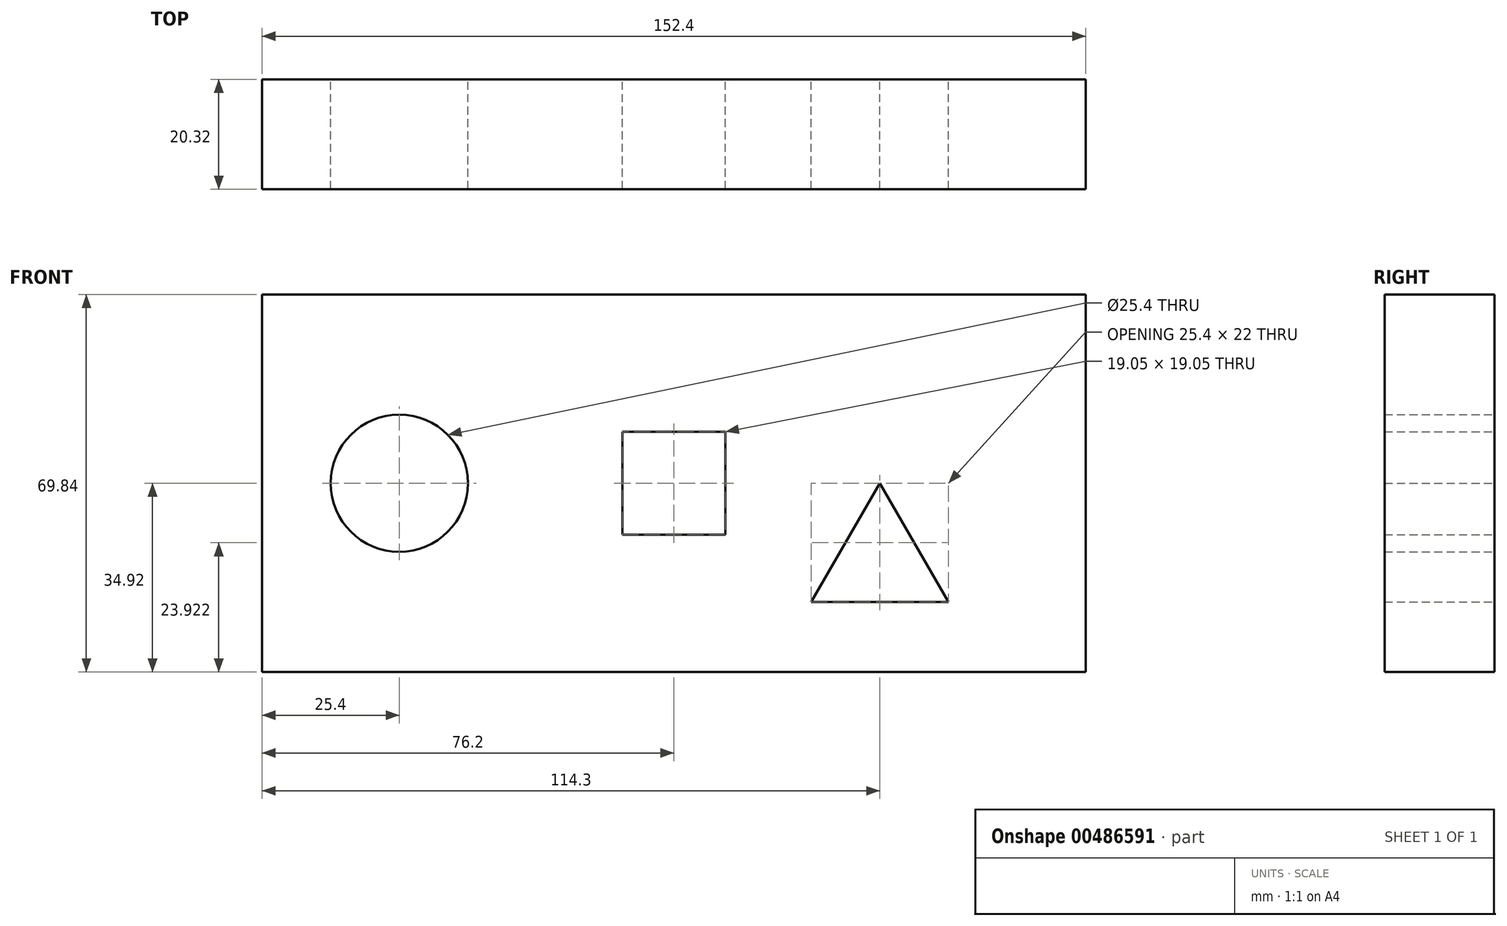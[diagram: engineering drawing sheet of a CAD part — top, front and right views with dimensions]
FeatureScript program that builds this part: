
annotation { "Feature Type Name" : "Feature", "Feature Type Description" : "" }
export const myFeature = defineFeature(function(context is Context, id is Id, definition is map)
    precondition{}
    {
        {
            var Q0;
            Q0=qCreatedBy(makeId("Front.planeOp"),FACE);
            var sketch = newSketch(context, id + "F0", { "sketchPlane" : qUnion([Q0])});
            skPoint(sketch, "E0", {"position": v(-31.75, 0) * mm});
            skPoint(sketch, "E1", {"position": v(-82.55, 0) * mm});
            skPoint(sketch, "E2", {"position": v(6.35, 0) * mm});
            skPoint(sketch, "E3", {"position": v(44.45, 0) * mm});
            skLineSegment(sketch, "E4.bottom", {"start": v(-22.22, 9.53) * mm, "end": v(-41.27, 9.53) * mm});
            skLineSegment(sketch, "E4.top", {"start": v(-22.22, -9.53) * mm, "end": v(-41.28, -9.52) * mm});
            skLineSegment(sketch, "E4.left", {"start": v(-22.22, 9.53) * mm, "end": v(-22.23, -9.53) * mm});
            skLineSegment(sketch, "E4.right", {"start": v(-41.27, 9.53) * mm, "end": v(-41.27, -9.52) * mm});
            skCircle(sketch, "E5", {"center": v(-82.55, 0) * mm, "radius": 12.7 * mm});
            skLineSegment(sketch, "E6", {"start": v(6.35, 0) * mm, "end": v(-6.35, -22) * mm});
            skLineSegment(sketch, "E7", {"start": v(-6.35, -22) * mm, "end": v(19.05, -22) * mm});
            skLineSegment(sketch, "E8", {"start": v(19.05, -22) * mm, "end": v(6.35, 0) * mm});
            skLineSegment(sketch, "E9.bottom", {"start": v(44.45, 34.92) * mm, "end": v(-107.95, 34.92) * mm});
            skLineSegment(sketch, "E9.top", {"start": v(44.45, -34.92) * mm, "end": v(-107.95, -34.92) * mm});
            skLineSegment(sketch, "E9.left", {"start": v(44.45, 34.92) * mm, "end": v(44.45, -34.92) * mm});
            skLineSegment(sketch, "E9.right", {"start": v(-107.95, 34.92) * mm, "end": v(-107.95, -34.92) * mm});
            skSolve(sketch);
        }
        {
            var Q0;
            Q0=makeQuery(id+"F0.imprint","IMPRINT",FACE,{"disambiguationData":[TD([[makeQuery(id+"F0.imprint","IMPRINT",EDGE,{"derivedFrom":sQuery(id+"F0.wireOp",EDGE,"E4.bottom")}),-1.0]])]});
            extrude(context, id + "F1", {"entities" : qUnion([Q0]), "depth" : 20.32 * mm});
        }
    });
